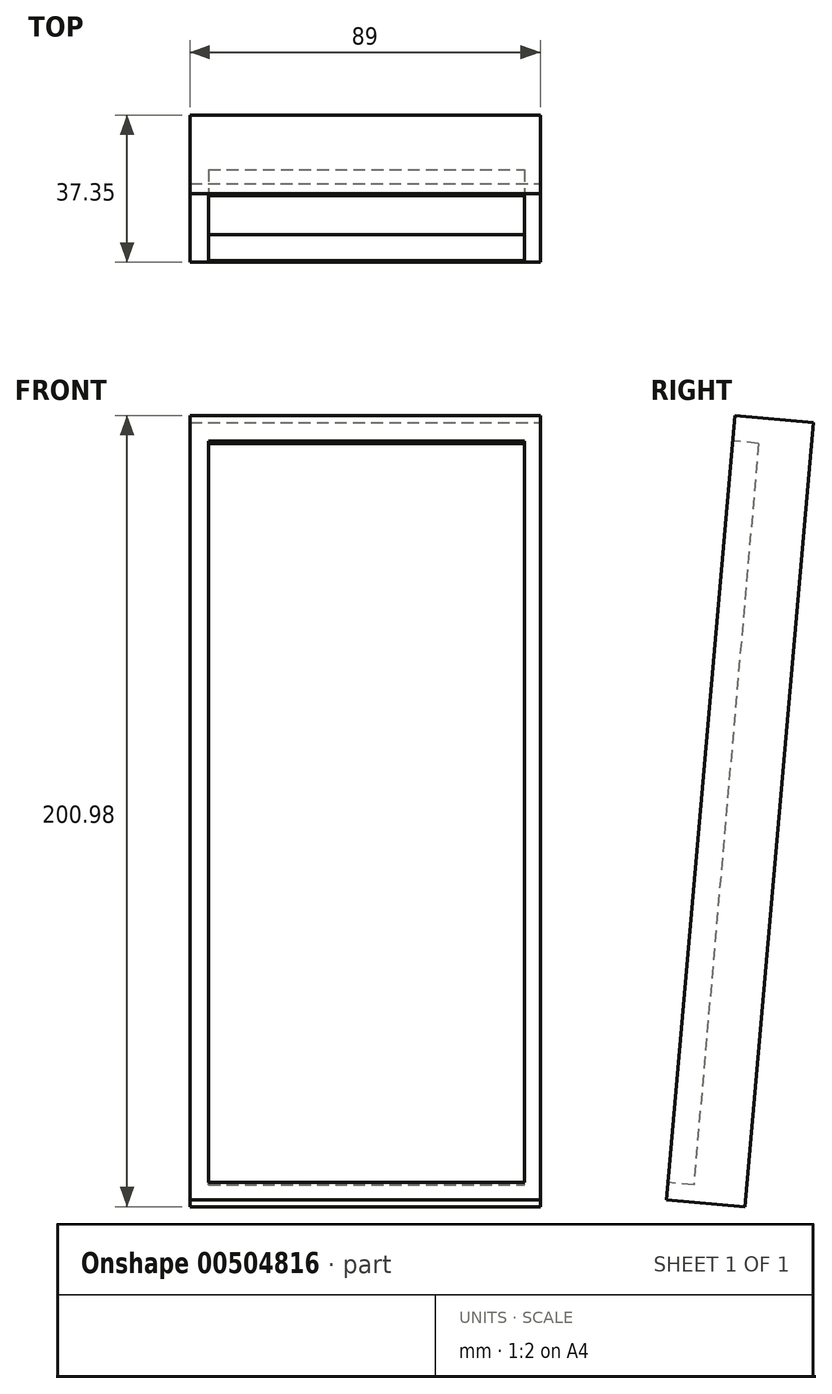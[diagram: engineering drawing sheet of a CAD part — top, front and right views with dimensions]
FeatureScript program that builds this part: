
annotation { "Feature Type Name" : "Feature", "Feature Type Description" : "" }
export const myFeature = defineFeature(function(context is Context, id is Id, definition is map)
    precondition{}
    {
        {
            var Q0;
            Q0=qCreatedBy(makeId("Top.planeOp"),FACE);
            var sketch = newSketch(context, id + "F0", { "sketchPlane" : qUnion([Q0])});
            skLineSegment(sketch, "E0.bottom", {"start": v(-387.06, 14.64) * mm, "end": v(57.94, 14.64) * mm});
            skLineSegment(sketch, "E0.top", {"start": v(-387.06, -85.36) * mm, "end": v(57.94, -85.36) * mm});
            skLineSegment(sketch, "E0.left", {"start": v(-387.06, 14.64) * mm, "end": v(-387.06, -85.36) * mm});
            skLineSegment(sketch, "E0.right", {"start": v(57.94, 14.64) * mm, "end": v(57.94, -85.36) * mm});
            skSolve(sketch);
        }
        {
            var Q0;
            Q0=makeQuery(id+"F0.imprint","IMPRINT",FACE,{"disambiguationData":[TD([[makeQuery(id+"F0.imprint","IMPRINT",EDGE,{"derivedFrom":sQuery(id+"F0.wireOp",EDGE,"E0.bottom")}),-1.0]])]});
            extrude(context, id + "F1", {"entities" : qUnion([Q0]), "depth" : 1000 * mm});
        }
        {
            var Q0;
            Q0=makeQuery(id+"F1.opExtrude","SWEPT_BODY",BODY,{"disambiguationData":[OSD([sQuery(id+"F0.wireOp",EDGE,"E0.bottom"),sQuery(id+"F0.wireOp",EDGE,"E0.top"),sQuery(id+"F0.wireOp",EDGE,"E0.left"),sQuery(id+"F0.wireOp",EDGE,"E0.right")])]});
            var Q1;
            Q1=makeQuery(id+"F1.opExtrude","CAP_EDGE",EDGE,{"disambiguationData":[OSD([sQuery(id+"F0.wireOp",EDGE,"E0.bottom")])],"isStart":true});
            var Q2;
            Q2=makeQuery(id+"F1.opExtrude","CAP_EDGE",EDGE,{"disambiguationData":[OSD([sQuery(id+"F0.wireOp",EDGE,"E0.bottom")])],"isStart":true});
            transform(context, id + "F2", {"entities" : qUnion([Q0]), "transformType" : TransformType.ROTATION, "transformAxis" : qUnion([Q2]), "angle" : 5 * degree, "oppositeDirection" : true, "makeCopy" : false});
        }
        {
            var Q0;
            Q0=makeQuery(id+"F1.opExtrude","SWEPT_BODY",BODY,{"disambiguationData":[OSD([sQuery(id+"F0.wireOp",EDGE,"E0.bottom"),sQuery(id+"F0.wireOp",EDGE,"E0.top"),sQuery(id+"F0.wireOp",EDGE,"E0.left"),sQuery(id+"F0.wireOp",EDGE,"E0.right")])]});
            var Q1;
            Q1=makeQuery(id+"F1.opExtrude","SWEPT_EDGE",EDGE,{"disambiguationData":[OSD([sQuery(id+"F0.wireOp",EDGE,"E0.top"),sQuery(id+"F0.wireOp",EDGE,"E0.right")])]});
            transform(context, id + "F3", {"entities" : qUnion([Q0]), "transformType" : TransformType.ROTATION, "transformAxis" : qUnion([Q1]), "angle" : 120 * degree, "oppositeDirection" : true, "makeCopy" : true});
        }
        {
            var Q0;
            Q0=makeQuery(id+"F3.opPattern","COPY",BODY,{"derivedFrom":makeQuery(id+"F1.opExtrude","SWEPT_BODY",BODY,{"disambiguationData":[OSD([sQuery(id+"F0.wireOp",EDGE,"E0.bottom"),sQuery(id+"F0.wireOp",EDGE,"E0.top"),sQuery(id+"F0.wireOp",EDGE,"E0.left"),sQuery(id+"F0.wireOp",EDGE,"E0.right")])]}),"instanceName":"1"});
            transform(context, id + "F4", {"entities" : qUnion([Q0]), "transformType" : TransformType.TRANSLATION_3D, "dx" : 87 * mm, "dy" : 55 * mm, "dz" : 0 * mm, "makeCopy" : false});
        }
        {
            var Q0;
            Q0=makeQuery(id+"F3.opPattern","COPY",BODY,{"derivedFrom":makeQuery(id+"F1.opExtrude","SWEPT_BODY",BODY,{"disambiguationData":[OSD([sQuery(id+"F0.wireOp",EDGE,"E0.bottom"),sQuery(id+"F0.wireOp",EDGE,"E0.top"),sQuery(id+"F0.wireOp",EDGE,"E0.left"),sQuery(id+"F0.wireOp",EDGE,"E0.right")])]}),"instanceName":"1"});
            var Q1;
            Q1=makeQuery(id+"F3.opPattern","COPY",EDGE,{"derivedFrom":makeQuery(id+"F1.opExtrude","SWEPT_EDGE",EDGE,{"disambiguationData":[OSD([sQuery(id+"F0.wireOp",EDGE,"E0.bottom"),sQuery(id+"F0.wireOp",EDGE,"E0.left")])]}),"instanceName":"1"});
            transform(context, id + "F5", {"entities" : qUnion([Q0]), "transformType" : TransformType.ROTATION, "transformAxis" : qUnion([Q1]), "angle" : 120 * degree, "oppositeDirection" : true, "makeCopy" : true});
        }
        {
            var Q0;
            Q0=makeQuery(id+"F5.opPattern","COPY",BODY,{"derivedFrom":makeQuery(id+"F3.opPattern","COPY",BODY,{"derivedFrom":makeQuery(id+"F1.opExtrude","SWEPT_BODY",BODY,{"disambiguationData":[OSD([sQuery(id+"F0.wireOp",EDGE,"E0.bottom"),sQuery(id+"F0.wireOp",EDGE,"E0.top"),sQuery(id+"F0.wireOp",EDGE,"E0.left"),sQuery(id+"F0.wireOp",EDGE,"E0.right")])]}),"instanceName":"1"}),"instanceName":"1"});
            transform(context, id + "F6", {"entities" : qUnion([Q0]), "transformType" : TransformType.TRANSLATION_3D, "dx" : 91 * mm, "dy" : -75 * mm, "dz" : 0 * mm, "makeCopy" : false});
        }
        {
            var Q0;
            Q0=makeQuery(id+"F3.opPattern","COPY",BODY,{"derivedFrom":makeQuery(id+"F1.opExtrude","SWEPT_BODY",BODY,{"disambiguationData":[OSD([sQuery(id+"F0.wireOp",EDGE,"E0.bottom"),sQuery(id+"F0.wireOp",EDGE,"E0.top"),sQuery(id+"F0.wireOp",EDGE,"E0.left"),sQuery(id+"F0.wireOp",EDGE,"E0.right")])]}),"instanceName":"1"});
            transform(context, id + "F7", {"entities" : qUnion([Q0]), "transformType" : TransformType.TRANSLATION_3D, "dx" : 13 * mm, "dy" : -17 * mm, "dz" : 0 * mm, "makeCopy" : false});
        }
        {
            var Q0;
            Q0=makeQuery(id+"F5.opPattern","COPY",BODY,{"derivedFrom":makeQuery(id+"F3.opPattern","COPY",BODY,{"derivedFrom":makeQuery(id+"F1.opExtrude","SWEPT_BODY",BODY,{"disambiguationData":[OSD([sQuery(id+"F0.wireOp",EDGE,"E0.bottom"),sQuery(id+"F0.wireOp",EDGE,"E0.top"),sQuery(id+"F0.wireOp",EDGE,"E0.left"),sQuery(id+"F0.wireOp",EDGE,"E0.right")])]}),"instanceName":"1"}),"instanceName":"1"});
            var Q1;
            Q1=makeQuery(id+"F5.opPattern","COPY",EDGE,{"derivedFrom":makeQuery(id+"F3.opPattern","COPY",EDGE,{"derivedFrom":makeQuery(id+"F1.opExtrude","SWEPT_EDGE",EDGE,{"disambiguationData":[OSD([sQuery(id+"F0.wireOp",EDGE,"E0.top"),sQuery(id+"F0.wireOp",EDGE,"E0.right")])]}),"instanceName":"1"}),"instanceName":"1"});
            transform(context, id + "F8", {"entities" : qUnion([Q0]), "transformType" : TransformType.ROTATION, "transformAxis" : qUnion([Q1]), "angle" : 120 * degree, "oppositeDirection" : true, "makeCopy" : true});
        }
        {
            var Q0;
            Q0=makeQuery(id+"F8.opPattern","COPY",BODY,{"derivedFrom":makeQuery(id+"F5.opPattern","COPY",BODY,{"derivedFrom":makeQuery(id+"F3.opPattern","COPY",BODY,{"derivedFrom":makeQuery(id+"F1.opExtrude","SWEPT_BODY",BODY,{"disambiguationData":[OSD([sQuery(id+"F0.wireOp",EDGE,"E0.bottom"),sQuery(id+"F0.wireOp",EDGE,"E0.top"),sQuery(id+"F0.wireOp",EDGE,"E0.left"),sQuery(id+"F0.wireOp",EDGE,"E0.right")])]}),"instanceName":"1"}),"instanceName":"1"}),"instanceName":"1"});
            transform(context, id + "F9", {"entities" : qUnion([Q0]), "transformType" : TransformType.TRANSLATION_3D, "dx" : -17 * mm, "dy" : -111 * mm, "dz" : 0 * mm, "makeCopy" : false});
        }
        {
            var Q0;
            Q0=makeQuery(id+"F8.opPattern","COPY",BODY,{"derivedFrom":makeQuery(id+"F5.opPattern","COPY",BODY,{"derivedFrom":makeQuery(id+"F3.opPattern","COPY",BODY,{"derivedFrom":makeQuery(id+"F1.opExtrude","SWEPT_BODY",BODY,{"disambiguationData":[OSD([sQuery(id+"F0.wireOp",EDGE,"E0.bottom"),sQuery(id+"F0.wireOp",EDGE,"E0.top"),sQuery(id+"F0.wireOp",EDGE,"E0.left"),sQuery(id+"F0.wireOp",EDGE,"E0.right")])]}),"instanceName":"1"}),"instanceName":"1"}),"instanceName":"1"});
            var Q1;
            Q1=makeQuery(id+"F8.opPattern","COPY",EDGE,{"derivedFrom":makeQuery(id+"F5.opPattern","COPY",EDGE,{"derivedFrom":makeQuery(id+"F3.opPattern","COPY",EDGE,{"derivedFrom":makeQuery(id+"F1.opExtrude","SWEPT_EDGE",EDGE,{"disambiguationData":[OSD([sQuery(id+"F0.wireOp",EDGE,"E0.bottom"),sQuery(id+"F0.wireOp",EDGE,"E0.left")])]}),"instanceName":"1"}),"instanceName":"1"}),"instanceName":"1"});
            transform(context, id + "F10", {"entities" : qUnion([Q0]), "transformType" : TransformType.ROTATION, "transformAxis" : qUnion([Q1]), "angle" : 120 * degree, "oppositeDirection" : true, "makeCopy" : true});
        }
        {
            var Q0;
            Q0=makeQuery(id+"F10.opPattern","COPY",BODY,{"derivedFrom":makeQuery(id+"F8.opPattern","COPY",BODY,{"derivedFrom":makeQuery(id+"F5.opPattern","COPY",BODY,{"derivedFrom":makeQuery(id+"F3.opPattern","COPY",BODY,{"derivedFrom":makeQuery(id+"F1.opExtrude","SWEPT_BODY",BODY,{"disambiguationData":[OSD([sQuery(id+"F0.wireOp",EDGE,"E0.bottom"),sQuery(id+"F0.wireOp",EDGE,"E0.top"),sQuery(id+"F0.wireOp",EDGE,"E0.left"),sQuery(id+"F0.wireOp",EDGE,"E0.right")])]}),"instanceName":"1"}),"instanceName":"1"}),"instanceName":"1"}),"instanceName":"1"});
            transform(context, id + "F11", {"entities" : qUnion([Q0]), "transformType" : TransformType.TRANSLATION_3D, "dx" : -104 * mm, "dy" : -42 * mm, "dz" : 0 * mm, "makeCopy" : false});
        }
        {
            var Q0;
            Q0=makeQuery(id+"F10.opPattern","COPY",BODY,{"derivedFrom":makeQuery(id+"F8.opPattern","COPY",BODY,{"derivedFrom":makeQuery(id+"F5.opPattern","COPY",BODY,{"derivedFrom":makeQuery(id+"F3.opPattern","COPY",BODY,{"derivedFrom":makeQuery(id+"F1.opExtrude","SWEPT_BODY",BODY,{"disambiguationData":[OSD([sQuery(id+"F0.wireOp",EDGE,"E0.bottom"),sQuery(id+"F0.wireOp",EDGE,"E0.top"),sQuery(id+"F0.wireOp",EDGE,"E0.left"),sQuery(id+"F0.wireOp",EDGE,"E0.right")])]}),"instanceName":"1"}),"instanceName":"1"}),"instanceName":"1"}),"instanceName":"1"});
            var Q1;
            Q1=makeQuery(id+"F10.opPattern","COPY",EDGE,{"derivedFrom":makeQuery(id+"F8.opPattern","COPY",EDGE,{"derivedFrom":makeQuery(id+"F5.opPattern","COPY",EDGE,{"derivedFrom":makeQuery(id+"F3.opPattern","COPY",EDGE,{"derivedFrom":makeQuery(id+"F1.opExtrude","SWEPT_EDGE",EDGE,{"disambiguationData":[OSD([sQuery(id+"F0.wireOp",EDGE,"E0.top"),sQuery(id+"F0.wireOp",EDGE,"E0.right")])]}),"instanceName":"1"}),"instanceName":"1"}),"instanceName":"1"}),"instanceName":"1"});
            transform(context, id + "F12", {"entities" : qUnion([Q0]), "transformType" : TransformType.ROTATION, "transformAxis" : qUnion([Q1]), "angle" : 120 * degree, "oppositeDirection" : true, "makeCopy" : true});
        }
        {
            var Q0;
            Q0=makeQuery(id+"F12.opPattern","COPY",BODY,{"derivedFrom":makeQuery(id+"F10.opPattern","COPY",BODY,{"derivedFrom":makeQuery(id+"F8.opPattern","COPY",BODY,{"derivedFrom":makeQuery(id+"F5.opPattern","COPY",BODY,{"derivedFrom":makeQuery(id+"F3.opPattern","COPY",BODY,{"derivedFrom":makeQuery(id+"F1.opExtrude","SWEPT_BODY",BODY,{"disambiguationData":[OSD([sQuery(id+"F0.wireOp",EDGE,"E0.bottom"),sQuery(id+"F0.wireOp",EDGE,"E0.top"),sQuery(id+"F0.wireOp",EDGE,"E0.left"),sQuery(id+"F0.wireOp",EDGE,"E0.right")])]}),"instanceName":"1"}),"instanceName":"1"}),"instanceName":"1"}),"instanceName":"1"}),"instanceName":"1"});
            transform(context, id + "F13", {"entities" : qUnion([Q0]), "transformType" : TransformType.TRANSLATION_3D, "dx" : -65 * mm, "dy" : 57 * mm, "dz" : 0 * mm, "makeCopy" : false});
        }
        {
            var Q0;
            Q0=makeQuery(id+"F1.opExtrude","SWEPT_FACE",FACE,{"disambiguationData":[OSD([sQuery(id+"F0.wireOp",EDGE,"E0.top")])]});
            var sketch = newSketch(context, id + "F14", { "sketchPlane" : qUnion([Q0])});
            skLineSegment(sketch, "E1.bottom", {"start": v(-363.51, 968.78) * mm, "end": v(37.85, 968.78) * mm});
            skLineSegment(sketch, "E1.top", {"start": v(-363.51, 23.2) * mm, "end": v(37.85, 23.2) * mm});
            skLineSegment(sketch, "E1.left", {"start": v(-363.51, 968.78) * mm, "end": v(-363.51, 23.2) * mm});
            skLineSegment(sketch, "E1.right", {"start": v(37.85, 968.78) * mm, "end": v(37.85, 23.2) * mm});
            skSolve(sketch);
        }
        {
            var Q0;
            Q0=makeQuery(id+"F14.imprint","IMPRINT",FACE,{"disambiguationData":[TD([[makeQuery(id+"F14.imprint","IMPRINT",EDGE,{"derivedFrom":sQuery(id+"F14.wireOp",EDGE,"E1.bottom")}),-1.0]])]});
            extrude(context, id + "F15", {"entities" : qUnion([Q0]), "operationType" : NewBodyOperationType.REMOVE, "oppositeDirection" : true, "depth" : 33 * mm});
        }
        {
            var Q0;
            Q0=makeQuery(id+"F5.opPattern","COPY",BODY,{"derivedFrom":makeQuery(id+"F3.opPattern","COPY",BODY,{"derivedFrom":makeQuery(id+"F1.opExtrude","SWEPT_BODY",BODY,{"disambiguationData":[OSD([sQuery(id+"F0.wireOp",EDGE,"E0.bottom"),sQuery(id+"F0.wireOp",EDGE,"E0.top"),sQuery(id+"F0.wireOp",EDGE,"E0.left"),sQuery(id+"F0.wireOp",EDGE,"E0.right")])]}),"instanceName":"1"}),"instanceName":"1"});
            var Q1;
            Q1=makeQuery(id+"F3.opPattern","COPY",BODY,{"derivedFrom":makeQuery(id+"F1.opExtrude","SWEPT_BODY",BODY,{"disambiguationData":[OSD([sQuery(id+"F0.wireOp",EDGE,"E0.bottom"),sQuery(id+"F0.wireOp",EDGE,"E0.top"),sQuery(id+"F0.wireOp",EDGE,"E0.left"),sQuery(id+"F0.wireOp",EDGE,"E0.right")])]}),"instanceName":"1"});
            var Q2;
            Q2=makeQuery(id+"F8.opPattern","COPY",BODY,{"derivedFrom":makeQuery(id+"F5.opPattern","COPY",BODY,{"derivedFrom":makeQuery(id+"F3.opPattern","COPY",BODY,{"derivedFrom":makeQuery(id+"F1.opExtrude","SWEPT_BODY",BODY,{"disambiguationData":[OSD([sQuery(id+"F0.wireOp",EDGE,"E0.bottom"),sQuery(id+"F0.wireOp",EDGE,"E0.top"),sQuery(id+"F0.wireOp",EDGE,"E0.left"),sQuery(id+"F0.wireOp",EDGE,"E0.right")])]}),"instanceName":"1"}),"instanceName":"1"}),"instanceName":"1"});
            var Q3;
            Q3=makeQuery(id+"F10.opPattern","COPY",BODY,{"derivedFrom":makeQuery(id+"F8.opPattern","COPY",BODY,{"derivedFrom":makeQuery(id+"F5.opPattern","COPY",BODY,{"derivedFrom":makeQuery(id+"F3.opPattern","COPY",BODY,{"derivedFrom":makeQuery(id+"F1.opExtrude","SWEPT_BODY",BODY,{"disambiguationData":[OSD([sQuery(id+"F0.wireOp",EDGE,"E0.bottom"),sQuery(id+"F0.wireOp",EDGE,"E0.top"),sQuery(id+"F0.wireOp",EDGE,"E0.left"),sQuery(id+"F0.wireOp",EDGE,"E0.right")])]}),"instanceName":"1"}),"instanceName":"1"}),"instanceName":"1"}),"instanceName":"1"});
            var Q4;
            Q4=makeQuery(id+"F12.opPattern","COPY",BODY,{"derivedFrom":makeQuery(id+"F10.opPattern","COPY",BODY,{"derivedFrom":makeQuery(id+"F8.opPattern","COPY",BODY,{"derivedFrom":makeQuery(id+"F5.opPattern","COPY",BODY,{"derivedFrom":makeQuery(id+"F3.opPattern","COPY",BODY,{"derivedFrom":makeQuery(id+"F1.opExtrude","SWEPT_BODY",BODY,{"disambiguationData":[OSD([sQuery(id+"F0.wireOp",EDGE,"E0.bottom"),sQuery(id+"F0.wireOp",EDGE,"E0.top"),sQuery(id+"F0.wireOp",EDGE,"E0.left"),sQuery(id+"F0.wireOp",EDGE,"E0.right")])]}),"instanceName":"1"}),"instanceName":"1"}),"instanceName":"1"}),"instanceName":"1"}),"instanceName":"1"});
            deleteBodies(context, id + "F16", {"entities" : qUnion([Q0, Q1, Q2, Q3, Q4])});
        }
        {
            var Q0;
            Q0=makeQuery(id+"F1.opExtrude","SWEPT_BODY",BODY,{"disambiguationData":[OSD([sQuery(id+"F0.wireOp",EDGE,"E0.bottom"),sQuery(id+"F0.wireOp",EDGE,"E0.top"),sQuery(id+"F0.wireOp",EDGE,"E0.left"),sQuery(id+"F0.wireOp",EDGE,"E0.right")])]});
            var Q1;
            Q1=makeQuery(id+"F1.opExtrude","CAP_VERTEX",VERTEX,{"disambiguationData":[OSD([sQuery(id+"F0.wireOp",EDGE,"E0.top"),sQuery(id+"F0.wireOp",EDGE,"E0.left")])],"isStart":true});
            transform(context, id + "F17", {"entities" : qUnion([Q0]), "transformType" : TransformType.SCALE_UNIFORMLY, "scale" : 1 / 5, "scalePoint" : qUnion([Q1]), "makeCopy" : false});
        }
    });
